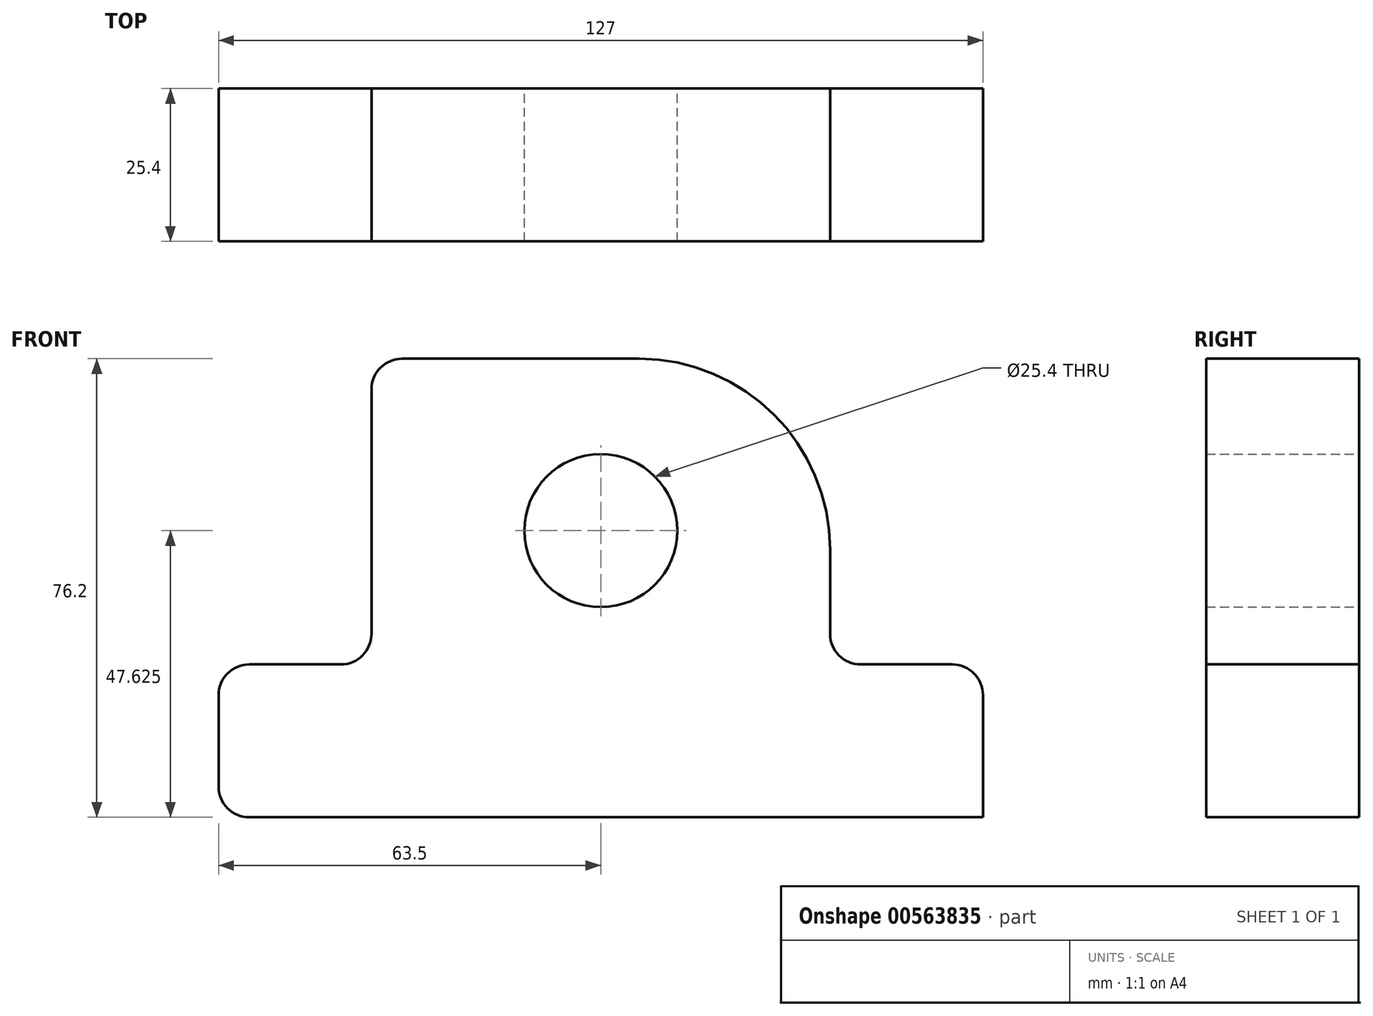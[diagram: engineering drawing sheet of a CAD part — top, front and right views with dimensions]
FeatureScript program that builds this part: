
annotation { "Feature Type Name" : "Feature", "Feature Type Description" : "" }
export const myFeature = defineFeature(function(context is Context, id is Id, definition is map)
    precondition{}
    {
        {
            var Q0;
            Q0=qCreatedBy(makeId("Front.planeOp"),FACE);
            var sketch = newSketch(context, id + "F0", { "sketchPlane" : qUnion([Q0])});
            skLineSegment(sketch, "E0.bottom", {"start": v(-63.5, 38.1) * mm, "end": v(63.5, 38.1) * mm});
            skLineSegment(sketch, "E0.top", {"start": v(-63.5, -38.1) * mm, "end": v(63.5, -38.1) * mm});
            skLineSegment(sketch, "E0.left", {"start": v(-63.5, 38.1) * mm, "end": v(-63.5, -38.1) * mm});
            skLineSegment(sketch, "E0.right", {"start": v(63.5, 38.1) * mm, "end": v(63.5, -38.1) * mm});
            skPoint(sketch, "E0.middle", {"position": v(0, 0) * mm});
            skLineSegment(sketch, "E1", {"start": v(-63.5, -38.1) * mm, "end": v(-63.5, -12.7) * mm});
            skLineSegment(sketch, "E2", {"start": v(-63.5, -12.7) * mm, "end": v(63.5, -12.7) * mm});
            skLineSegment(sketch, "E3", {"start": v(-63.5, -12.7) * mm, "end": v(0, -12.7) * mm});
            skLineSegment(sketch, "E4", {"start": v(0, -12.7) * mm, "end": v(-38.1, -12.7) * mm});
            skLineSegment(sketch, "E5", {"start": v(-38.1, -12.7) * mm, "end": v(38.1, -12.7) * mm});
            skLineSegment(sketch, "E6", {"start": v(38.1, -12.7) * mm, "end": v(38.1, 38.1) * mm});
            skLineSegment(sketch, "E7", {"start": v(-38.1, -12.7) * mm, "end": v(-38.1, 38.1) * mm});
            skSolve(sketch);
        }
        {
            var Q0;
            {var subQ0=sQuery(id+"F0.wireOp",EDGE,"E6");Q0=makeQuery(id+"F0.imprint","IMPRINT",FACE,{"disambiguationData":[TD([[makeQuery(id+"F0.imprint","IMPRINT",EDGE,{"derivedFrom":subQ0}),1.0]])]});}
            var Q1;
            {var subQ1=sQuery(id+"F0.wireOp",EDGE,"E0.top");Q1=makeQuery(id+"F0.imprint","IMPRINT",FACE,{"disambiguationData":[TD([[makeQuery(id+"F0.imprint","IMPRINT",EDGE,{"derivedFrom":subQ1}),1.0]])]});}
            extrude(context, id + "F1", {"entities" : qUnion([Q0, Q1]), "endBound" : BoundingType.SYMMETRIC, "depth" : 25.4 * mm, "offsetDistance" : 25.4 * mm});
        }
        {
            var Q0;
            Q0=makeQuery(id+"F1.opExtrude","SWEPT_EDGE",EDGE,{"disambiguationData":[OSD([sQuery(id+"F0.wireOp",EDGE,"E0.left"),sQuery(id+"F0.wireOp",EDGE,"E1"),sQuery(id+"F0.wireOp",EDGE,"E3")])]});
            var Q1;
            Q1=makeQuery(id+"F1.opExtrude","SWEPT_EDGE",EDGE,{"disambiguationData":[OSD([sQuery(id+"F0.wireOp",EDGE,"E0.right"),sQuery(id+"F0.wireOp",EDGE,"E2")])]});
            var Q2;
            Q2=makeQuery(id+"F1.opExtrude","SWEPT_EDGE",EDGE,{"disambiguationData":[OSD([sQuery(id+"F0.wireOp",EDGE,"E3"),sQuery(id+"F0.wireOp",EDGE,"E5"),sQuery(id+"F0.wireOp",EDGE,"E7")])]});
            var Q3;
            Q3=makeQuery(id+"F1.opExtrude","SWEPT_EDGE",EDGE,{"disambiguationData":[OSD([sQuery(id+"F0.wireOp",EDGE,"E2"),sQuery(id+"F0.wireOp",EDGE,"E5"),sQuery(id+"F0.wireOp",EDGE,"E6")])]});
            fillet(context, id + "F2", {"entities" : qUnion([Q0, Q1, Q2, Q3]), "radius" : 5.08 * mm, "tangentPropagation" : true, "allowEdgeOverflow" : false});
        }
        {
            var Q0;
            Q0=makeQuery(id+"F1.opExtrude","SWEPT_EDGE",EDGE,{"disambiguationData":[OSD([sQuery(id+"F0.wireOp",EDGE,"E0.bottom"),sQuery(id+"F0.wireOp",EDGE,"E7")])]});
            var Q1;
            Q1=makeQuery(id+"F1.opExtrude","SWEPT_EDGE",EDGE,{"disambiguationData":[OSD([sQuery(id+"F0.wireOp",EDGE,"E0.bottom"),sQuery(id+"F0.wireOp",EDGE,"E6")])]});
            fillet(context, id + "F3", {"entities" : qUnion([Q0, Q1]), "radius" : 31.75 * mm, "tangentPropagation" : true, "allowEdgeOverflow" : false});
        }
        {
            var Q0;
            Q0=qCreatedBy(makeId("Front.planeOp"),FACE);
            var sketch = newSketch(context, id + "F4", { "sketchPlane" : qUnion([Q0])});
            skLineSegment(sketch, "E8", {"start": v(0, 0) * mm, "end": v(0, 9.53) * mm});
            skCircle(sketch, "E9", {"center": v(0, 9.53) * mm, "radius": 12.7 * mm});
            skSolve(sketch);
        }
        {
            var Q0;
            Q0 = qSketchRegion(id + "F4", true);
            extrude(context, id + "F5", {"entities" : qUnion([Q0]), "operationType" : NewBodyOperationType.REMOVE, "endBound" : BoundingType.SYMMETRIC, "depth" : 50.8 * mm, "offsetDistance" : 25.4 * mm});
        }
    });
